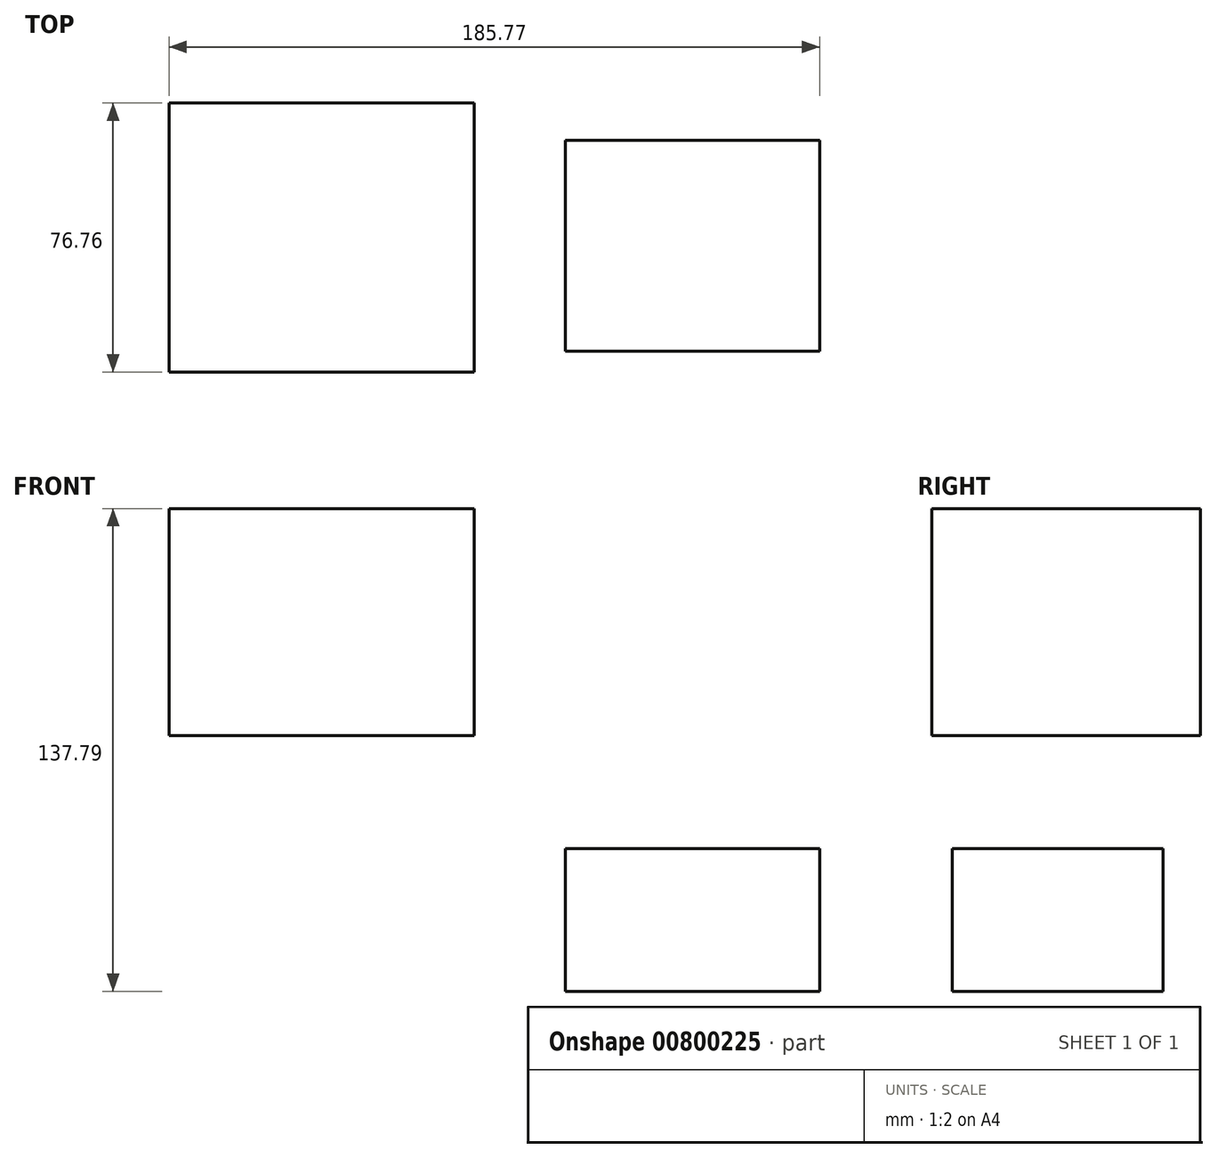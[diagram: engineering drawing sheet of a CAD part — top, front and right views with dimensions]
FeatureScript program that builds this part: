
annotation { "Feature Type Name" : "Feature", "Feature Type Description" : "" }
export const myFeature = defineFeature(function(context is Context, id is Id, definition is map)
    precondition{}
    {
        {
            var Q0;
            Q0=qCreatedBy(makeId("Top.planeOp"),FACE);
            var sketch = newSketch(context, id + "F0", { "sketchPlane" : qUnion([Q0])});
            skLineSegment(sketch, "E0.bottom", {"start": v(-113.13, 30.31) * mm, "end": v(-26.01, 30.31) * mm});
            skLineSegment(sketch, "E0.top", {"start": v(-113.13, -46.45) * mm, "end": v(-26.01, -46.45) * mm});
            skLineSegment(sketch, "E0.left", {"start": v(-113.13, 30.31) * mm, "end": v(-113.13, -46.45) * mm});
            skLineSegment(sketch, "E0.right", {"start": v(-26.01, 30.31) * mm, "end": v(-26.01, -46.45) * mm});
            skSolve(sketch);
        }
        {
            var Q0;
            Q0=makeQuery(id+"F0.imprint","IMPRINT",FACE,{"disambiguationData":[TD([[makeQuery(id+"F0.imprint","IMPRINT",EDGE,{"derivedFrom":sQuery(id+"F0.wireOp",EDGE,"E0.bottom")}),-1.0]])]});
            extrude(context, id + "F1", {"entities" : qUnion([Q0]), "depth" : 64.77 * mm, "offsetDistance" : 25.4 * mm});
        }
        {
            var Q0;
            Q0=qCreatedBy(makeId("Right.planeOp"),FACE);
            var sketch = newSketch(context, id + "F2", { "sketchPlane" : qUnion([Q0])});
            skLineSegment(sketch, "E1.bottom", {"start": v(19.7, -32.25) * mm, "end": v(-40.54, -32.25) * mm});
            skLineSegment(sketch, "E1.top", {"start": v(19.7, -73.02) * mm, "end": v(-40.54, -73.02) * mm});
            skLineSegment(sketch, "E1.left", {"start": v(19.7, -32.25) * mm, "end": v(19.7, -73.02) * mm});
            skLineSegment(sketch, "E1.right", {"start": v(-40.54, -32.25) * mm, "end": v(-40.54, -73.02) * mm});
            skSolve(sketch);
        }
        {
            var Q0;
            Q0=makeQuery(id+"F2.imprint","IMPRINT",FACE,{"disambiguationData":[TD([[makeQuery(id+"F2.imprint","IMPRINT",EDGE,{"derivedFrom":sQuery(id+"F2.wireOp",EDGE,"E1.bottom")}),1.0]])]});
            extrude(context, id + "F3", {"entities" : qUnion([Q0]), "depth" : 72.64 * mm, "offsetDistance" : 25.4 * mm});
        }
    });
